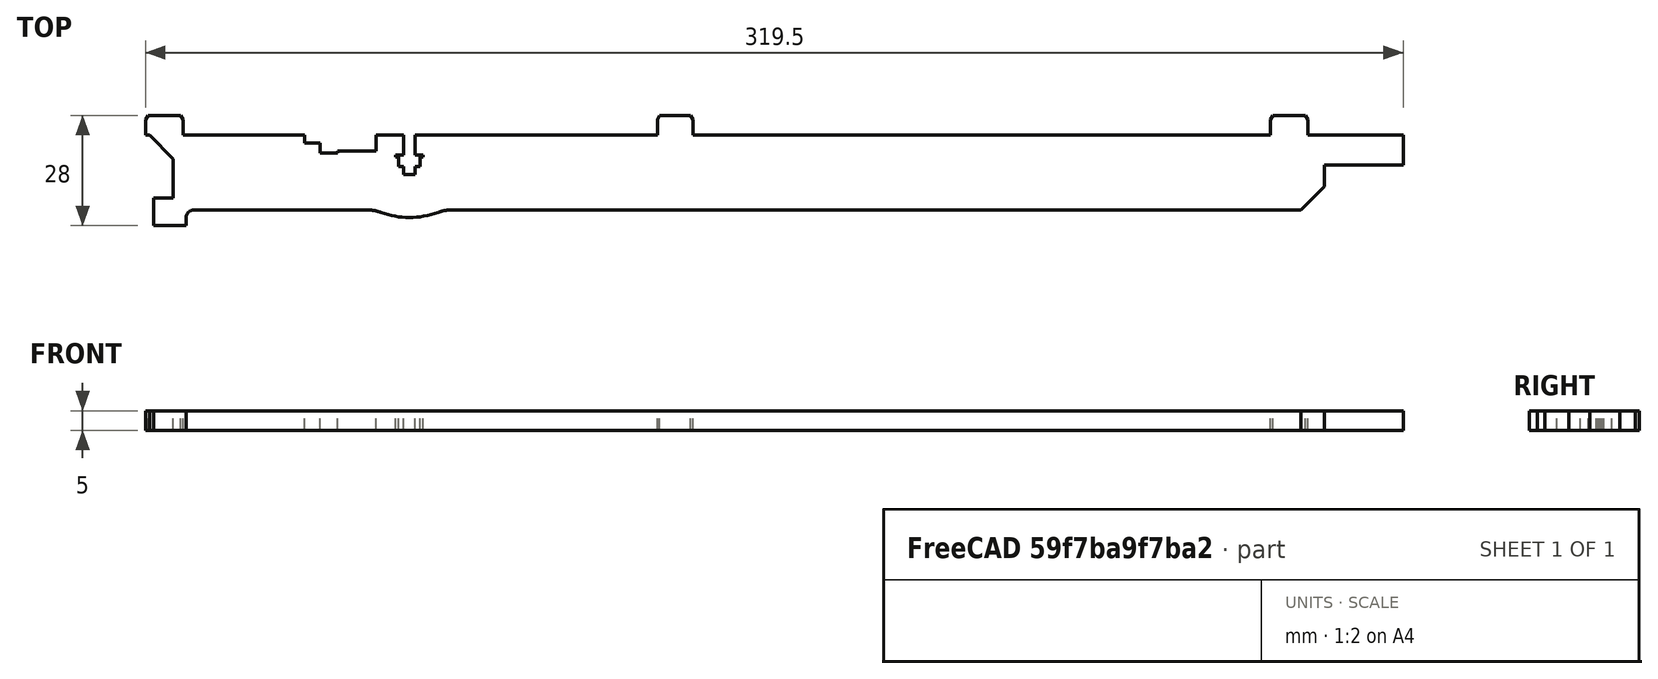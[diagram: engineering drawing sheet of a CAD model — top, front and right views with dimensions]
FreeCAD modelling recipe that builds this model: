
FCSTD DOCUMENT  (FreeCAD 0.17R13541 (Git))
Label: xx_xxx_x-rib
License: All rights reserved
LicenseURL: http://en.wikipedia.org/wiki/All_rights_reserved
objects: Sketcher::SketchObject×1, PartDesign::Pad×1, PartDesign::Body×1
note: 4 computed .brp shape members not serialized (recipe doc carries the construction recipe); baked Part::Feature solids carry a one-line shape summary decoded from their .brp

FEATURE [Sketcher::SketchObject] Sketch059
  MapMode = 5
  Support = -> [XY_Plane]
  sketch-geometry (59):
    g0: LineSegment StartX=-4.25 StartY=11.6 StartZ=0 EndX=-4.82735 EndY=12.6 EndZ=0
    g1: LineSegment StartX=-233.98 StartY=-2.4 StartZ=0 EndX=-233.98 EndY=-0.4 EndZ=0
    g2: ArcOfCircle CenterX=-287.271 CenterY=-13.4 CenterZ=0 NormalX=0 NormalY=0 NormalZ=1 AngleXU=0 Radius=2 StartAngle=1.5708 EndAngle=3.14159
    g3: LineSegment StartX=0 StartY=0 StartZ=0 EndX=20 EndY=0 EndZ=0
    g4: LineSegment StartX=-169.5 StartY=7.6 StartZ=0 EndX=-231.02 EndY=7.6 EndZ=0
    g5: LineSegment StartX=-287.271 StartY=-11.4 StartZ=0 EndX=-243.201 EndY=-11.4 EndZ=0
    g6: LineSegment StartX=-259.093 StartY=7.6 StartZ=0 EndX=-290 EndY=7.6 EndZ=0
    g7: LineSegment StartX=-297.5 StartY=-8.4 StartZ=0 EndX=-297.5 EndY=-15.4 EndZ=0
    g8: LineSegment StartX=-290.577 StartY=12.6 StartZ=0 EndX=-298.923 EndY=12.6 EndZ=0
    g9: LineSegment StartX=-236 StartY=2.1 StartZ=0 EndX=-236 EndY=2.6 EndZ=0
    g10: LineSegment StartX=-250.8 StartY=3.6 StartZ=0 EndX=-250.8 EndY=3.1 EndZ=0
    g11: LineSegment StartX=-233.98 StartY=-0.4 StartZ=0 EndX=-235.25 EndY=-0.4 EndZ=0
    g12: LineSegment StartX=-231.02 StartY=2.6 StartZ=0 EndX=-229 EndY=2.6 EndZ=0
    g13: LineSegment StartX=-289.271 StartY=-13.4 StartZ=0 EndX=-289.271 EndY=-15.4 EndZ=0
    g14: LineSegment StartX=-168.923 StartY=12.6 StartZ=0 EndX=-169.5 EndY=11.6 EndZ=0
    g15: ArcOfCircle CenterX=-221.799 CenterY=-21.4 CenterZ=0 NormalX=0 NormalY=0 NormalZ=1 AngleXU=0 Radius=10 StartAngle=1.5708 EndAngle=1.92428
    g16: LineSegment StartX=-6 StartY=-11.4 StartZ=0 EndX=0 EndY=-5.4 EndZ=0
    g17: LineSegment StartX=-259.093 StartY=5.6 StartZ=0 EndX=-259.093 EndY=7.6 EndZ=0
    g18: LineSegment StartX=-233.98 StartY=2.6 StartZ=0 EndX=-233.98 EndY=7.6 EndZ=0
    g19: LineSegment StartX=-13.75 StartY=7.6 StartZ=0 EndX=-160.5 EndY=7.6 EndZ=0
    g20: LineSegment StartX=-299.5 StartY=11.6 StartZ=0 EndX=-299.5 EndY=7.6 EndZ=0
    g21: LineSegment StartX=0 StartY=-5.4 StartZ=0 EndX=0 EndY=0 EndZ=0
    g22: LineSegment StartX=-229.75 StartY=2.1 StartZ=0 EndX=-229.75 EndY=-0.4 EndZ=0
    g23: LineSegment StartX=-160.5 StartY=7.6 StartZ=0 EndX=-160.5 EndY=11.6 EndZ=0
    g24: LineSegment StartX=-250.8 StartY=3.1 StartZ=0 EndX=-255.2 EndY=3.1 EndZ=0
    g25: LineSegment StartX=-231.02 StartY=-2.4 StartZ=0 EndX=-233.98 EndY=-2.4 EndZ=0
    g26: LineSegment StartX=-229 StartY=2.1 StartZ=0 EndX=-229.75 EndY=2.1 EndZ=0
    g27: LineSegment StartX=-4.82735 StartY=12.6 StartZ=0 EndX=-13.1726 EndY=12.6 EndZ=0
    g28: LineSegment StartX=-169.5 StartY=11.6 StartZ=0 EndX=-169.5 EndY=7.6 EndZ=0
    g29: LineSegment StartX=-289.271 StartY=-15.4 StartZ=0 EndX=-297.5 EndY=-15.4 EndZ=0
    g30: ArcOfCircle CenterX=-232.5 CenterY=7.6 CenterZ=0 NormalX=0 NormalY=0 NormalZ=1 AngleXU=0 Radius=20.9112 StartAngle=4.3589 EndAngle=5.06587
    g31: ArcOfCircle CenterX=-243.201 CenterY=-21.4 CenterZ=0 NormalX=0 NormalY=0 NormalZ=1 AngleXU=0 Radius=10 StartAngle=1.21731 EndAngle=1.5708
    g32: LineSegment StartX=-233.98 StartY=7.6 StartZ=0 EndX=-241 EndY=7.6 EndZ=0
    g33: LineSegment StartX=-13.1726 StartY=12.6 StartZ=0 EndX=-13.75 EndY=11.6 EndZ=0
    g34: LineSegment StartX=-290 StartY=11.6 StartZ=0 EndX=-290.577 EndY=12.6 EndZ=0
    g35: LineSegment StartX=-161.077 StartY=12.6 StartZ=0 EndX=-168.923 EndY=12.6 EndZ=0
    g36: LineSegment StartX=-231.02 StartY=-0.4 StartZ=0 EndX=-231.02 EndY=-2.4 EndZ=0
    g37: LineSegment StartX=-160.5 StartY=11.6 StartZ=0 EndX=-161.077 EndY=12.6 EndZ=0
    g38: LineSegment StartX=-231.02 StartY=7.6 StartZ=0 EndX=-231.02 EndY=2.6 EndZ=0
    g39: LineSegment StartX=-255.2 StartY=5.6 StartZ=0 EndX=-259.093 EndY=5.6 EndZ=0
    g40: LineSegment StartX=-229.75 StartY=-0.4 StartZ=0 EndX=-231.02 EndY=-0.4 EndZ=0
    g41: LineSegment StartX=-235.25 StartY=-0.4 StartZ=0 EndX=-235.25 EndY=2.1 EndZ=0
    g42: LineSegment StartX=-229 StartY=2.6 StartZ=0 EndX=-229 EndY=2.1 EndZ=0
    g43: LineSegment StartX=-299.5 StartY=7.6 StartZ=0 EndX=-298.5 EndY=7.6 EndZ=0
    g44: LineSegment StartX=-241 StartY=3.6 StartZ=0 EndX=-250.8 EndY=3.6 EndZ=0
    g45: LineSegment StartX=-235.25 StartY=2.1 StartZ=0 EndX=-236 EndY=2.1 EndZ=0
    g46: LineSegment StartX=-292.5 StartY=1.6 StartZ=0 EndX=-292.5 EndY=-8.4 EndZ=0
    g47: LineSegment StartX=-255.2 StartY=3.1 StartZ=0 EndX=-255.2 EndY=5.6 EndZ=0
    g48: LineSegment StartX=-236 StartY=2.6 StartZ=0 EndX=-233.98 EndY=2.6 EndZ=0
    g49: LineSegment StartX=-292.5 StartY=-8.4 StartZ=0 EndX=-297.5 EndY=-8.4 EndZ=0
    g50: LineSegment StartX=-241 StartY=7.6 StartZ=0 EndX=-241 EndY=3.6 EndZ=0
    g51: LineSegment StartX=-4.25 StartY=7.6 StartZ=0 EndX=-4.25 EndY=11.6 EndZ=0
    g52: LineSegment StartX=-290 StartY=7.6 StartZ=0 EndX=-290 EndY=11.6 EndZ=0
    g53: LineSegment StartX=-298.5 StartY=7.6 StartZ=0 EndX=-292.5 EndY=1.6 EndZ=0
    g54: LineSegment StartX=20 StartY=0 StartZ=0 EndX=20 EndY=7.6 EndZ=0
    g55: LineSegment StartX=20 StartY=7.6 StartZ=0 EndX=-4.25 EndY=7.6 EndZ=0
    g56: LineSegment StartX=-298.923 StartY=12.6 StartZ=0 EndX=-299.5 EndY=11.6 EndZ=0
    g57: LineSegment StartX=-13.75 StartY=11.6 StartZ=0 EndX=-13.75 EndY=7.6 EndZ=0
    g58: LineSegment StartX=-221.799 StartY=-11.4 StartZ=0 EndX=-6 EndY=-11.4 EndZ=0
  constraints (59):
    c: Coincident(g20,g43)
    c: Coincident(g56,g20)
    c: Coincident(g56,g8)
    c: Coincident(g43,g53)
    c: Coincident(g29,g7)
    c: Coincident(g49,g7)
    c: Coincident(g46,g49)
    c: Coincident(g53,g46)
    c: Coincident(g8,g34)
    c: Coincident(g6,g52)
    c: Coincident(g34,g52)
    c: Coincident(g13,g29)
    c: Coincident(g13,g2)
    c: Coincident(g2,g5)
    c: Coincident(g17,g39)
    c: Coincident(g17,g6)
    c: Coincident(g24,g47)
    c: Coincident(g39,g47)
    c: Coincident(g24,g10)
    c: Coincident(g44,g10)
    c: Coincident(g31,g5)
    c: Coincident(g44,g50)
    c: Coincident(g32,g50)
    c: Coincident(g31,g30)
    c: Coincident(g9,g45)
    c: Coincident(g48,g9)
    c: Coincident(g11,g41)
    c: Coincident(g41,g45)
    c: Coincident(g25,g1)
    c: Coincident(g1,g11)
    c: Coincident(g18,g48)
    c: Coincident(g18,g32)
    c: Coincident(g25,g36)
    c: Coincident(g36,g40)
    c: Coincident(g12,g38)
    c: Coincident(g4,g38)
    c: Coincident(g40,g22)
    c: Coincident(g22,g26)
    c: Coincident(g26,g42)
    c: Coincident(g42,g12)
    c: Coincident(g15,g30)
    c: Coincident(g15,g58)
    c: Coincident(g28,g4)
    c: Coincident(g28,g14)
    c: Coincident(g35,g14)
    c: Coincident(g37,g35)
    c: Coincident(g19,g23)
    c: Coincident(g23,g37)
    c: Coincident(g57,g19)
    c: Coincident(g33,g57)
    c: Coincident(g33,g27)
    c: Coincident(g58,g16)
    c: Coincident(g27,g0)
    c: Coincident(g51,g55)
    c: Coincident(g51,g0)
    c: Coincident(g21,g16)
    c: Coincident(g21,g3)
    c: Coincident(g54,g3)
    c: Coincident(g54,g55)
FEATURE [PartDesign::Pad] Pad
  Length = 5
  Length2 = 100
  Profile = -> Sketch059
  Type = 0
FEATURE [PartDesign::Body] Body
  Group = -> [Sketch059,Pad]
  Origin = -> Origin
  Tip = -> Pad
